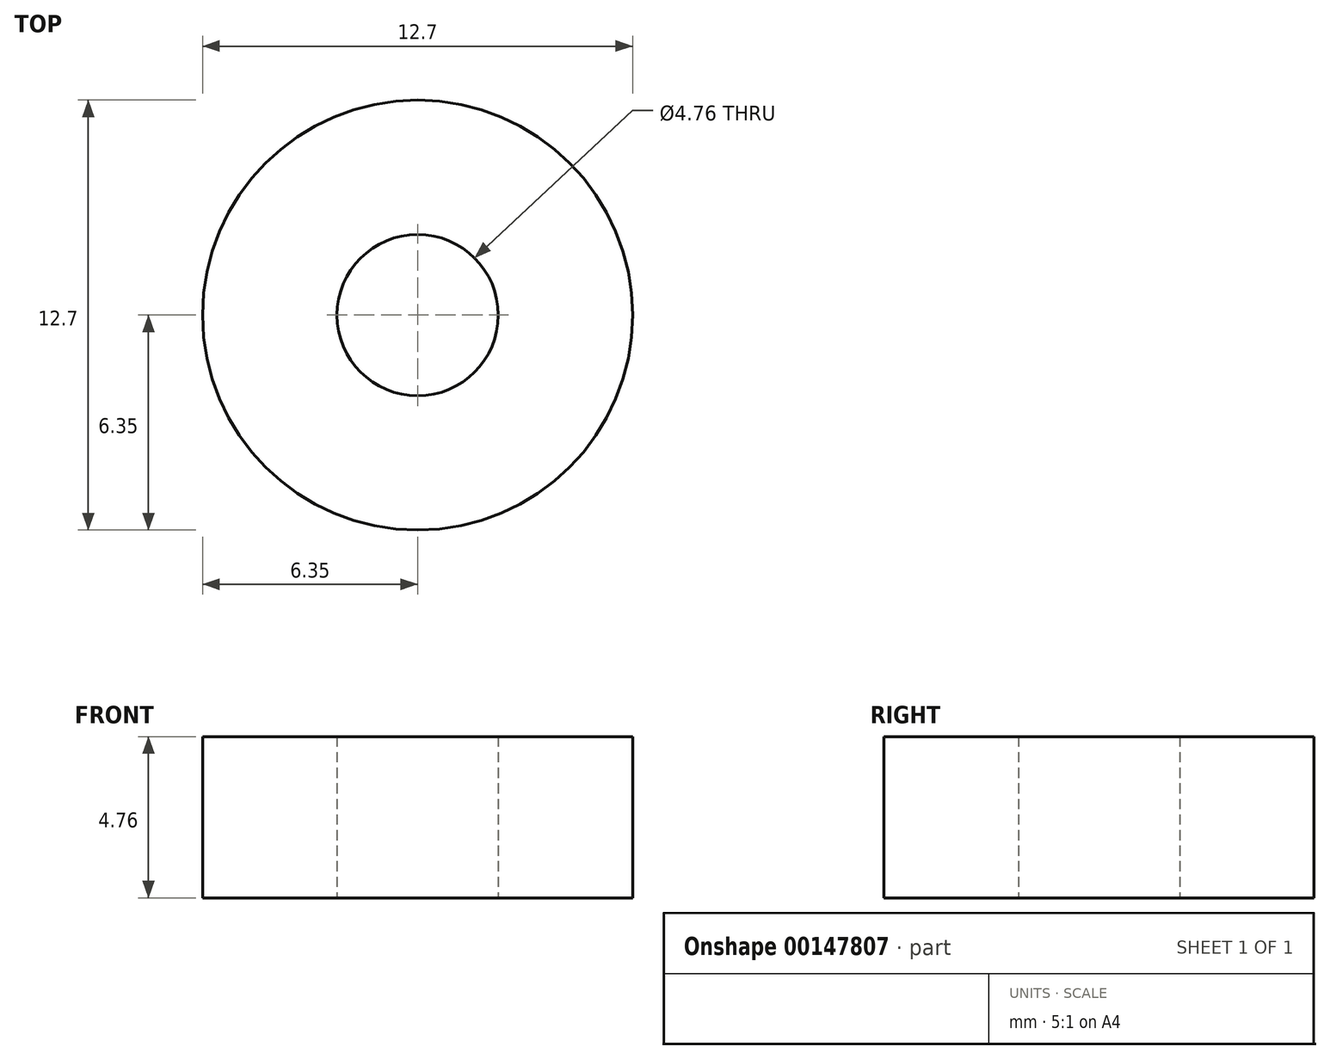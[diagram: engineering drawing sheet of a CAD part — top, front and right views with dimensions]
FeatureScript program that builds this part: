
annotation { "Feature Type Name" : "Feature", "Feature Type Description" : "" }
export const myFeature = defineFeature(function(context is Context, id is Id, definition is map)
    precondition{}
    {
        {
            var Q0;
            Q0=qCreatedBy(makeId("Top.planeOp"),FACE);
            var sketch = newSketch(context, id + "F0", { "sketchPlane" : qUnion([Q0])});
            skCircle(sketch, "E0", {"center": v(0, 0) * mm, "radius": 2.38 * mm});
            skCircle(sketch, "E1", {"center": v(0, 0) * mm, "radius": 6.35 * mm});
            skSolve(sketch);
        }
        {
            var Q0;
            Q0=qSketchRegion(id+"F0",true);
            extrude(context, id + "F1", {"entities" : qUnion([Q0]), "depth" : 4.76 * mm});
        }
    });
